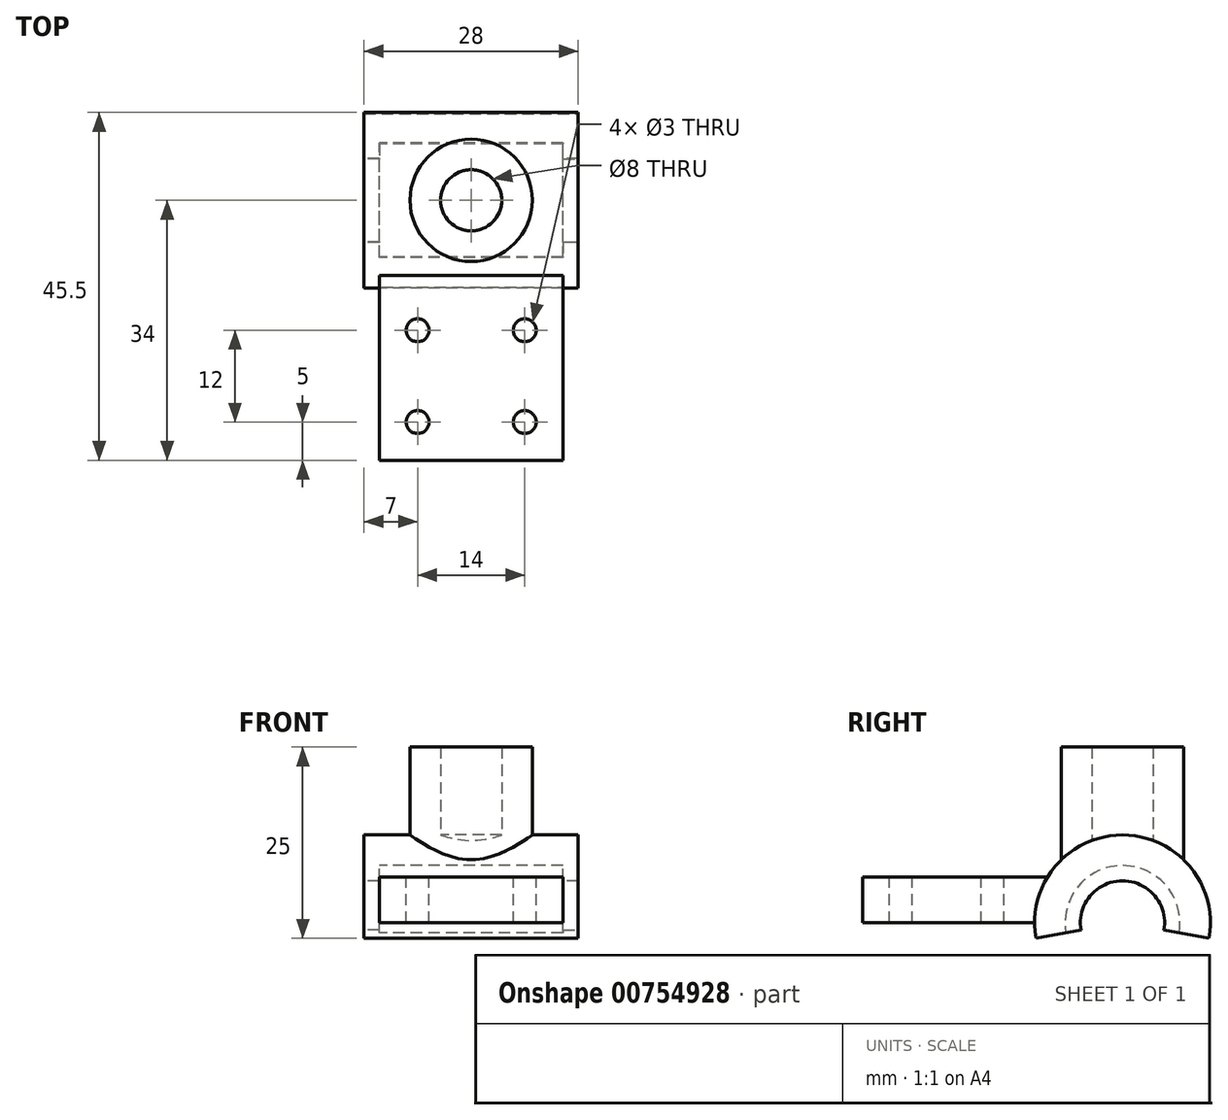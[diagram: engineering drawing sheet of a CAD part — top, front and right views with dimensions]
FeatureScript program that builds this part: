
annotation { "Feature Type Name" : "Feature", "Feature Type Description" : "" }
export const myFeature = defineFeature(function(context is Context, id is Id, definition is map)
    precondition{}
    {
        {
            var Q0;
            Q0=qCreatedBy(makeId("Front.planeOp"),FACE);
            var sketch = newSketch(context, id + "F0", { "sketchPlane" : qUnion([Q0])});
            skLineSegment(sketch, "E0", {"start": v(0, 0) * mm, "end": v(0, 7.5) * mm});
            skLineSegment(sketch, "E1", {"start": v(0, 7.5) * mm, "end": v(-24, 7.5) * mm});
            skLineSegment(sketch, "E2", {"start": v(-24, 7.5) * mm, "end": v(-24, 5.5) * mm});
            skLineSegment(sketch, "E3", {"start": v(-24, 5.5) * mm, "end": v(-26, 5.5) * mm});
            skLineSegment(sketch, "E4", {"start": v(-26, 5.5) * mm, "end": v(-26, 11.5) * mm});
            skLineSegment(sketch, "E5", {"start": v(-26, 11.5) * mm, "end": v(2, 11.5) * mm});
            skLineSegment(sketch, "E6", {"start": v(2, 11.5) * mm, "end": v(2, 5.5) * mm});
            skLineSegment(sketch, "E7", {"start": v(0, 5.5) * mm, "end": v(2, 5.5) * mm});
            skLineSegment(sketch, "E8", {"start": v(-34.2, 0) * mm, "end": v(6.7, 0) * mm, "construction": true});
            skSolve(sketch);
        }
        {
            var Q0;
            {var subQ0=sQuery(id+"F0.wireOp",EDGE,"E1");Q0=makeQuery(id+"F0.imprint","IMPRINT",FACE,{"disambiguationData":[TD([[makeQuery(id+"F0.imprint","IMPRINT",EDGE,{"derivedFrom":subQ0}),-1.0]])]});}
            var Q1;
            Q1=sQuery(id+"F0.wireOp",EDGE,"E8");
            revolve(context, id + "F1", {"surfaceOperationType" : NewSurfaceOperationType.NEW, "entities" : qUnion([Q0]), "axis" : qUnion([Q1]), "revolveType" : RevolveType.SYMMETRIC, "angle" : 200 * degree});
        }
        {
            var Q0;
            Q0=qCreatedBy(makeId("Top.planeOp"),FACE);
            cPlane(context, id + "F2", {"entities" : qUnion([Q0]), "cplaneType" : CPlaneType.OFFSET, "offset" : 8 * mm, "width" : 150 * mm, "height" : 150 * mm});
        }
        {
            var Q0;
            Q0=qCreatedBy(id+"F2.planeOp",FACE);
            var sketch = newSketch(context, id + "F3", { "sketchPlane" : qUnion([Q0])});
            skLineSegment(sketch, "E9", {"start": v(0, 0) * mm, "end": v(-12, 0) * mm});
            skCircle(sketch, "E10", {"center": v(-12, 0) * mm, "radius": 4 * mm});
            skCircle(sketch, "E11", {"center": v(-12, 0) * mm, "radius": 8 * mm});
            skSolve(sketch);
        }
        {
            var Q0;
            Q0 = qSketchRegion(id + "F3", true);
            extrude(context, id + "F4", {"entities" : qUnion([Q0]), "operationType" : NewBodyOperationType.ADD, "depth" : 15 * mm, "offsetDistance" : 25 * mm});
        }
        {
            var Q0;
            Q0=qCreatedBy(makeId("Front.planeOp"),FACE);
            cPlane(context, id + "F5", {"entities" : qUnion([Q0]), "cplaneType" : CPlaneType.OFFSET, "offset" : 9 * mm, "width" : 150 * mm, "height" : 150 * mm});
        }
        {
            var Q0;
            Q0=qCreatedBy(id+"F5.planeOp",FACE);
            var sketch = newSketch(context, id + "F6", { "sketchPlane" : qUnion([Q0])});
            skLineSegment(sketch, "E12.bottom", {"start": v(0, 0) * mm, "end": v(-24, 0) * mm});
            skLineSegment(sketch, "E12.top", {"start": v(0, 6) * mm, "end": v(-24, 6) * mm});
            skLineSegment(sketch, "E12.left", {"start": v(0, 0) * mm, "end": v(0, 6) * mm});
            skLineSegment(sketch, "E12.right", {"start": v(-24, 0) * mm, "end": v(-24, 6) * mm});
            skSolve(sketch);
        }
        {
            var Q0;
            Q0 = qSketchRegion(id + "F6", true);
            extrude(context, id + "F7", {"entities" : qUnion([Q0]), "operationType" : NewBodyOperationType.ADD, "depth" : 25 * mm, "offsetDistance" : 25 * mm});
        }
        {
            var Q0;
            Q0=makeQuery(id+"F7.opExtrude","SWEPT_FACE",FACE,{"disambiguationData":[OSD([sQuery(id+"F6.wireOp",EDGE,"E12.top")])]});
            var sketch = newSketch(context, id + "F8", { "sketchPlane" : qUnion([Q0])});
            skLineSegment(sketch, "E13", {"start": v(-24, -21.9) * mm, "end": v(0, -21.9) * mm, "construction": true});
            skLineSegment(sketch, "E14", {"start": v(-12, -34) * mm, "end": v(-12, -11) * mm, "construction": true});
            skLineSegment(sketch, "E15.0", {"start": v(-19, -34) * mm, "end": v(-19, -9.81) * mm});
            skLineSegment(sketch, "E16.0", {"start": v(0, -29) * mm, "end": v(-24, -29) * mm});
            skLineSegment(sketch, "E17.0", {"start": v(-5, -34) * mm, "end": v(-5, -9.81) * mm});
            skPoint(sketch, "E18", {"position": v(-19, -29) * mm});
            skPoint(sketch, "E19", {"position": v(-5, -29) * mm});
            skLineSegment(sketch, "E20.0", {"start": v(0, -17) * mm, "end": v(-24, -17) * mm});
            skPoint(sketch, "E21", {"position": v(-19, -17) * mm});
            skPoint(sketch, "E22", {"position": v(-5, -17) * mm});
            skSolve(sketch);
        }
        {
            var Q0;
            Q0=sQuery(id+"F8.wireOp",VERTEX,"E18");
            var Q1;
            Q1=sQuery(id+"F8.wireOp",VERTEX,"E19");
            var Q2;
            Q2=sQuery(id+"F8.wireOp",VERTEX,"E22");
            var Q3;
            Q3=sQuery(id+"F8.wireOp",VERTEX,"E21");
            var Q4;
            Q4=makeQuery(id+"F1.opRevolve","SWEPT_BODY",BODY,{"disambiguationData":[OSD([sQuery(id+"F0.wireOp",EDGE,"E0"),sQuery(id+"F0.wireOp",EDGE,"E1"),sQuery(id+"F0.wireOp",EDGE,"E2"),sQuery(id+"F0.wireOp",EDGE,"E3"),sQuery(id+"F0.wireOp",EDGE,"E4"),sQuery(id+"F0.wireOp",EDGE,"E5"),sQuery(id+"F0.wireOp",EDGE,"E6"),sQuery(id+"F0.wireOp",EDGE,"E7")])]});
            hole(context, id + "F9", {"style" : HoleStyle.SIMPLE, "endStyle" : HoleEndStyle.BLIND, "holeDiameter" : 3 * mm, "majorDiameter" : 5 * mm, "holeDepth" : 10 * mm, "isTappedThrough" : true, "tappedDepth" : 8 * mm, "tapClearance" : 3, "startFromSketch" : true, "locations" : qUnion([Q0, Q1, Q2, Q3]), "scope" : qUnion([Q4])});
        }
    });
